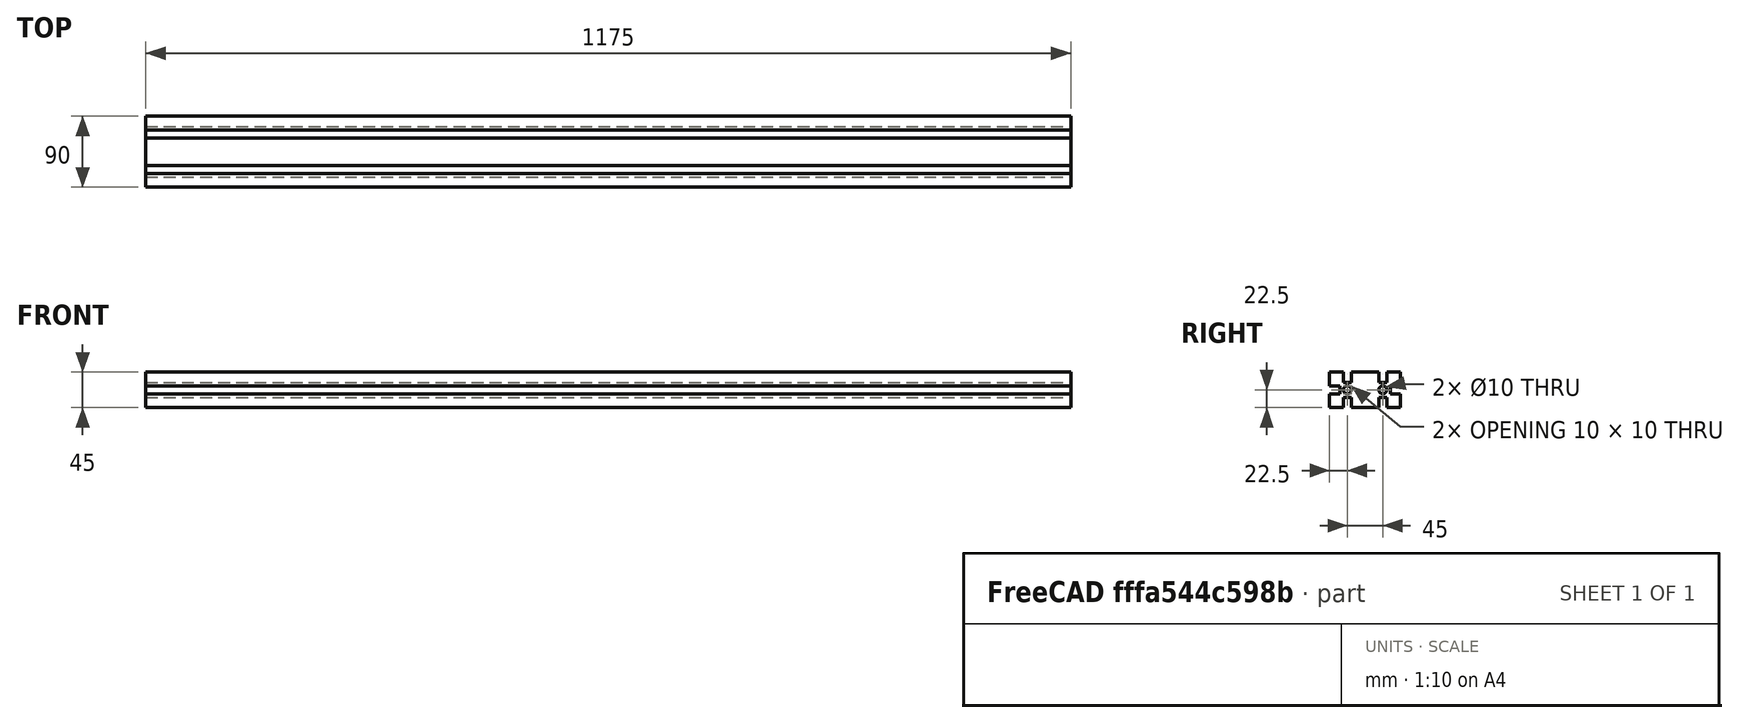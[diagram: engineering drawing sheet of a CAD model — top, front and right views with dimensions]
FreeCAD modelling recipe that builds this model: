
FCSTD DOCUMENT  (FreeCAD 1.0R39109 (Git))
Label: vslot 45x90x1175
License: All rights reserved
LicenseURL: https://en.wikipedia.org/wiki/All_rights_reserved
objects: PartDesign::Pad×2, Part::Feature×1, PartDesign::FeatureBase×1, PartDesign::Body×1
note: 10 computed .brp shape members not serialized (recipe doc carries the construction recipe); baked Part::Feature solids carry a one-line shape summary decoded from their .brp

FEATURE [Part::Feature] Part__Feature  label="1"
  shape: bbox 1000 x 90 x 45 mm, 34 faces (baked)
FEATURE [PartDesign::FeatureBase] BaseFeature
  BaseFeature = -> Part__Feature
  Suppressed = false
FEATURE [PartDesign::Pad] Pad
  BaseFeature = -> BaseFeature
  Direction = (1,0,0)
  Length = 80
  Length2 = 10
  Profile = -> BaseFeature [Face34]
  Refine = true
  Suppressed = false
  Type = 0
FEATURE [PartDesign::Pad] Pad001
  BaseFeature = -> Pad
  Direction = (1,0,0)
  Length = 95
  Length2 = 10
  Profile = -> Pad [Face3]
  Refine = true
  Suppressed = false
  Type = 0
FEATURE [PartDesign::Body] Body
  AllowCompound = false
  BaseFeature = -> Part__Feature
  Group = -> [BaseFeature,Pad,Pad001]
  Origin = -> Origin
  Tip = -> Pad001
